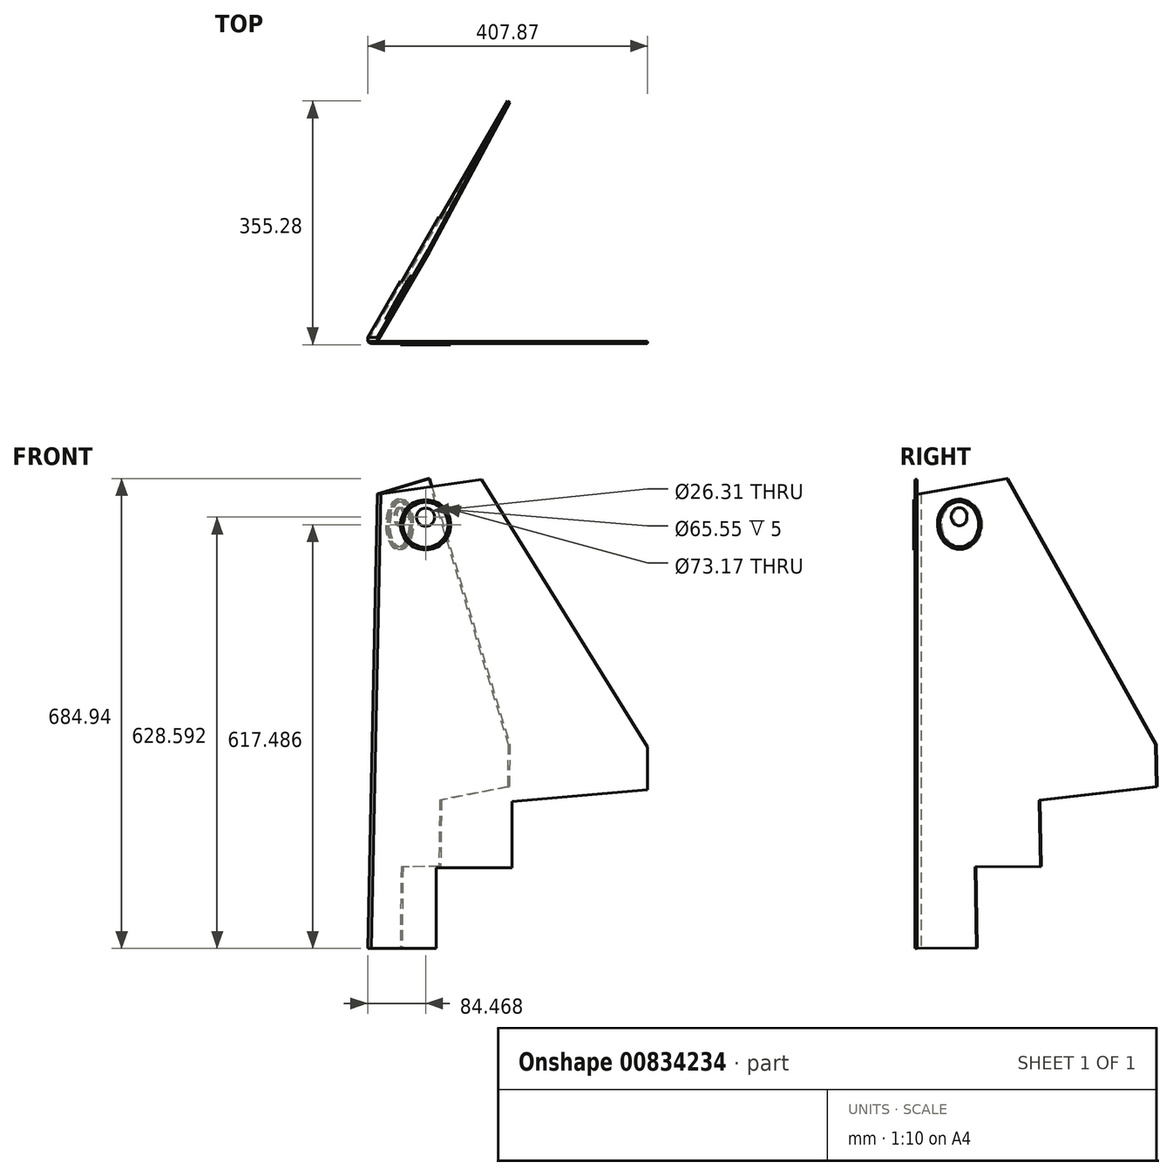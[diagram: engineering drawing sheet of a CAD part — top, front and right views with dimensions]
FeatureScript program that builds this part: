
annotation { "Feature Type Name" : "Feature", "Feature Type Description" : "" }
export const myFeature = defineFeature(function(context is Context, id is Id, definition is map)
    precondition{}
    {
        {
            var Q0;
            Q0=qCreatedBy(makeId("Front.planeOp"),FACE);
            var sketch = newSketch(context, id + "F0", { "sketchPlane" : qUnion([Q0])});
            skLineSegment(sketch, "E0", {"start": v(-139.4, 314.76) * mm, "end": v(7.2, 335.26) * mm});
            skLineSegment(sketch, "E1", {"start": v(7.2, 335.26) * mm, "end": v(249.18, -54.63) * mm});
            skLineSegment(sketch, "E2", {"start": v(249.18, -54.63) * mm, "end": v(249.18, -116.57) * mm});
            skLineSegment(sketch, "E3", {"start": v(249.18, -116.57) * mm, "end": v(51.58, -133.84) * mm});
            skLineSegment(sketch, "E4", {"start": v(51.58, -133.84) * mm, "end": v(51.58, -230.35) * mm});
            skLineSegment(sketch, "E5", {"start": v(51.58, -230.35) * mm, "end": v(-58.55, -230.35) * mm});
            skLineSegment(sketch, "E6", {"start": v(-58.55, -230.35) * mm, "end": v(-58.55, -348) * mm});
            skLineSegment(sketch, "E7", {"start": v(-58.55, -348) * mm, "end": v(-153.6, -348) * mm});
            skLineSegment(sketch, "E8", {"start": v(-153.6, -348) * mm, "end": v(-139.4, 314.76) * mm});
            skLineSegment(sketch, "E9", {"start": v(7.2, 335.26) * mm, "end": v(7.2, -350.54) * mm});
            skCircle(sketch, "E10", {"center": v(-74.22, 269.49) * mm, "radius": 32.77 * mm});
            skCircle(sketch, "E11", {"center": v(-74.22, 280.6) * mm, "radius": 13.15 * mm});
            skCircle(sketch, "E12.0", {"center": v(-74.22, 269.49) * mm, "radius": 36.58 * mm});
            skLineSegment(sketch, "E13", {"start": v(-144.42, 314.06) * mm, "end": v(-158.6, -348) * mm});
            skLineSegment(sketch, "E14", {"start": v(-158.6, -348) * mm, "end": v(-153.6, -348) * mm});
            skLineSegment(sketch, "E15", {"start": v(-139.4, 314.76) * mm, "end": v(-144.42, 314.06) * mm});
            skSolve(sketch);
        }
        {
            var Q0;
            Q0 = qSketchRegion(id + "F0", true);
            extrude(context, id + "F1", {"entities" : qUnion([Q0]), "depth" : 3 * mm, "offsetDistance" : 25 * mm});
        }
        {
            var Q0;
            Q0=makeQuery(id+"F0.imprint","IMPRINT",FACE,{"disambiguationData":[TD([[makeQuery(id+"F0.imprint","IMPRINT",EDGE,{"derivedFrom":sQuery(id+"F0.wireOp",EDGE,"E10")}),1.0]])]});
            extrude(context, id + "F2", {"entities" : qUnion([Q0]), "depth" : 3 * mm, "offsetDistance" : 25 * mm});
        }
        {
            var Q0;
            Q0=makeQuery(id+"F0.imprint","IMPRINT",FACE,{"disambiguationData":[TD([[makeQuery(id+"F0.imprint","IMPRINT",EDGE,{"derivedFrom":sQuery(id+"F0.wireOp",EDGE,"E10")}),-1.0]])]});
            var Q1;
            Q1=makeQuery(id+"F0.imprint","IMPRINT",FACE,{"disambiguationData":[TD([[makeQuery(id+"F0.imprint","IMPRINT",EDGE,{"derivedFrom":sQuery(id+"F0.wireOp",EDGE,"E11")}),1.0]])]});
            extrude(context, id + "F3", {"entities" : qUnion([Q0, Q1]), "depth" : 5 * mm, "offsetDistance" : 25 * mm});
        }
        {
            var Q0;
            Q0=makeQuery(id+"F1.opExtrude","CAP_EDGE",EDGE,{"disambiguationData":[OSD([sQuery(id+"F0.wireOp",EDGE,"E13")])],"isStart":false});
            chamfer(context, id + "F4", {"entities" : qUnion([Q0]), "chamferType" : ChamferType.OFFSET_ANGLE, "width" : 5 * mm, "oppositeDirection" : false, "angle" : 30 * degree, "tangentPropagation" : true});
        }
        {
            var Q0;
            Q0=makeQuery(id+"F1.opExtrude","SWEPT_BODY",BODY,{"disambiguationData":[OSD([sQuery(id+"F0.wireOp",EDGE,"E0"),sQuery(id+"F0.wireOp",EDGE,"E1"),sQuery(id+"F0.wireOp",EDGE,"E2"),sQuery(id+"F0.wireOp",EDGE,"E3"),sQuery(id+"F0.wireOp",EDGE,"E4"),sQuery(id+"F0.wireOp",EDGE,"E5"),sQuery(id+"F0.wireOp",EDGE,"E6"),sQuery(id+"F0.wireOp",EDGE,"E7"),sQuery(id+"F0.wireOp",EDGE,"E12.0"),sQuery(id+"F0.wireOp",EDGE,"E13"),sQuery(id+"F0.wireOp",EDGE,"E14"),sQuery(id+"F0.wireOp",EDGE,"E15")])]});
            var Q1;
            Q1=makeQuery(id+"F2.opExtrude","SWEPT_BODY",BODY,{"disambiguationData":[OSD([sQuery(id+"F0.wireOp",EDGE,"E10"),sQuery(id+"F0.wireOp",EDGE,"E11")])]});
            var Q2;
            Q2=makeQuery(id+"F3.opExtrude","SWEPT_BODY",BODY,{"disambiguationData":[OSD([sQuery(id+"F0.wireOp",EDGE,"E11")])]});
            var Q3;
            Q3=makeQuery(id+"F3.opExtrude","SWEPT_BODY",BODY,{"disambiguationData":[OSD([sQuery(id+"F0.wireOp",EDGE,"E10"),sQuery(id+"F0.wireOp",EDGE,"E12.0")])]});
            var Q4;
            Q4=makeQuery(id+"F1.opExtrude","SWEPT_FACE",FACE,{"disambiguationData":[OSD([sQuery(id+"F0.wireOp",EDGE,"E13")])]});
            mirror(context, id + "F5", {"entities" : qUnion([Q0, Q1, Q2, Q3]), "mirrorPlane" : qUnion([Q4])});
        }
        {
            var Q0;
            Q0=makeQuery(id+"F5.opPattern","COPY",BODY,{"derivedFrom":makeQuery(id+"F1.opExtrude","SWEPT_BODY",BODY,{"disambiguationData":[OSD([sQuery(id+"F0.wireOp",EDGE,"E0"),sQuery(id+"F0.wireOp",EDGE,"E1"),sQuery(id+"F0.wireOp",EDGE,"E2"),sQuery(id+"F0.wireOp",EDGE,"E3"),sQuery(id+"F0.wireOp",EDGE,"E4"),sQuery(id+"F0.wireOp",EDGE,"E5"),sQuery(id+"F0.wireOp",EDGE,"E6"),sQuery(id+"F0.wireOp",EDGE,"E7"),sQuery(id+"F0.wireOp",EDGE,"E12.0"),sQuery(id+"F0.wireOp",EDGE,"E13"),sQuery(id+"F0.wireOp",EDGE,"E14"),sQuery(id+"F0.wireOp",EDGE,"E15")])]}),"instanceName":"1"});
            var Q1;
            Q1=makeQuery(id+"F5.opPattern","COPY",BODY,{"derivedFrom":makeQuery(id+"F2.opExtrude","SWEPT_BODY",BODY,{"disambiguationData":[OSD([sQuery(id+"F0.wireOp",EDGE,"E10"),sQuery(id+"F0.wireOp",EDGE,"E11")])]}),"instanceName":"1"});
            var Q2;
            Q2=makeQuery(id+"F5.opPattern","COPY",BODY,{"derivedFrom":makeQuery(id+"F3.opExtrude","SWEPT_BODY",BODY,{"disambiguationData":[OSD([sQuery(id+"F0.wireOp",EDGE,"E10"),sQuery(id+"F0.wireOp",EDGE,"E12.0")])]}),"instanceName":"1"});
            var Q3;
            Q3=makeQuery(id+"F5.opPattern","COPY",BODY,{"derivedFrom":makeQuery(id+"F3.opExtrude","SWEPT_BODY",BODY,{"disambiguationData":[OSD([sQuery(id+"F0.wireOp",EDGE,"E11")])]}),"instanceName":"1"});
            var Q4;
            Q4=sQuery(id+"F0.wireOp",EDGE,"E13");
            transform(context, id + "F6", {"entities" : qUnion([Q0, Q1, Q2, Q3]), "transformType" : TransformType.ROTATION, "transformAxis" : qUnion([Q4]), "angle" : 120 * degree, "makeCopy" : false});
        }
    });
